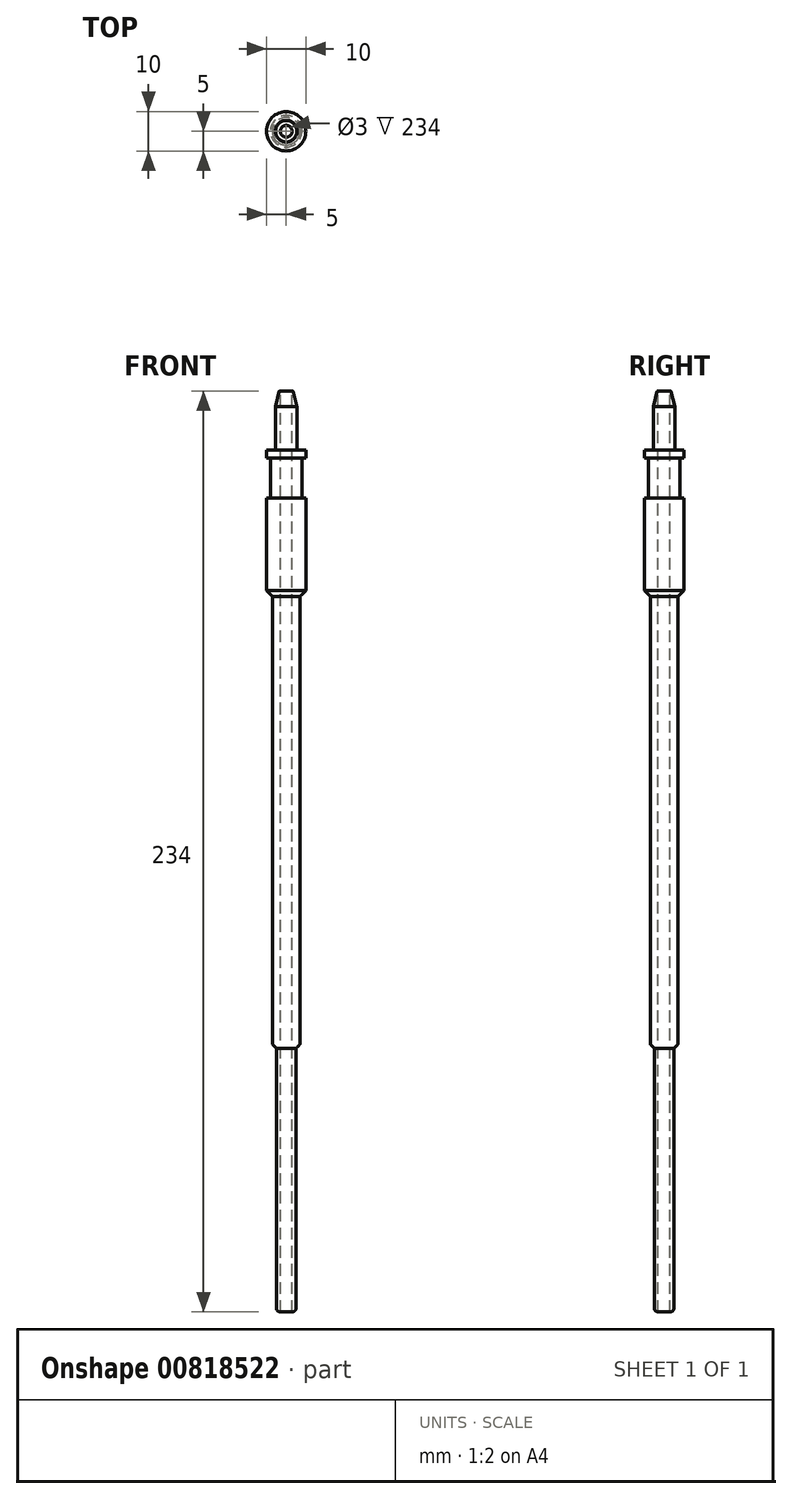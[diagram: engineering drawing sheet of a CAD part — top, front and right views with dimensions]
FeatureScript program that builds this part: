
annotation { "Feature Type Name" : "Feature", "Feature Type Description" : "" }
export const myFeature = defineFeature(function(context is Context, id is Id, definition is map)
    precondition{}
    {
        {
            var Q0;
            Q0=qCreatedBy(makeId("Front.planeOp"),FACE);
            var sketch = newSketch(context, id + "F0", { "sketchPlane" : qUnion([Q0])});
            skLineSegment(sketch, "E0", {"start": v(-1.5, 29.44) * mm, "end": v(-2.75, 28.44) * mm});
            skLineSegment(sketch, "E1", {"start": v(-2.75, 28.44) * mm, "end": v(-2.75, 14.44) * mm});
            skLineSegment(sketch, "E2", {"start": v(-2.75, 14.44) * mm, "end": v(-5, 14.44) * mm});
            skLineSegment(sketch, "E3", {"start": v(-5, 14.44) * mm, "end": v(-5, 12.44) * mm});
            skLineSegment(sketch, "E4", {"start": v(-5, 12.44) * mm, "end": v(-4, 12.44) * mm});
            skLineSegment(sketch, "E5", {"start": v(-4, 12.44) * mm, "end": v(-4, 2.24) * mm});
            skLineSegment(sketch, "E6", {"start": v(-4, 2.24) * mm, "end": v(-5, 2.24) * mm});
            skLineSegment(sketch, "E7", {"start": v(-5, 2.24) * mm, "end": v(-5, -22.26) * mm});
            skLineSegment(sketch, "E8", {"start": v(-5, -22.26) * mm, "end": v(-3.5, -23.26) * mm});
            skLineSegment(sketch, "E9", {"start": v(-3.5, -23.26) * mm, "end": v(-3.5, -136.56) * mm});
            skLineSegment(sketch, "E10", {"start": v(-3.5, -136.56) * mm, "end": v(-2.5, -137.56) * mm});
            skLineSegment(sketch, "E11", {"start": v(-2.5, -137.56) * mm, "end": v(-2.5, -204.56) * mm});
            skLineSegment(sketch, "E12", {"start": v(0, 30.64) * mm, "end": v(0, -204.56) * mm, "construction": true});
            skLineSegment(sketch, "E13", {"start": v(0, 30.64) * mm, "end": v(0, -204.56) * mm});
            skLineSegment(sketch, "E14", {"start": v(-1.5, 29.44) * mm, "end": v(-1.5, -204.56) * mm});
            skLineSegment(sketch, "E15", {"start": v(-2.5, -204.56) * mm, "end": v(0, -204.56) * mm});
            skPoint(sketch, "E16.orphan", {"position": v(0, -205.56) * mm});
            skLineSegment(sketch, "E17", {"start": v(-1.5, 29.44) * mm, "end": v(-2.75, 29.44) * mm});
            skLineSegment(sketch, "E18", {"start": v(-2.75, 29.44) * mm, "end": v(-2.75, 28.44) * mm});
            skLineSegment(sketch, "E19", {"start": v(-5, -22.26) * mm, "end": v(-5, -23.26) * mm});
            skLineSegment(sketch, "E20", {"start": v(-5, -23.26) * mm, "end": v(-3.5, -23.26) * mm});
            skSolve(sketch);
        }
        {
            var Q0;
            {var subQ0=sQuery(id+"F0.wireOp",EDGE,"E1");Q0=makeQuery(id+"F0.imprint","IMPRINT",FACE,{"disambiguationData":[TD([[makeQuery(id+"F0.imprint","IMPRINT",EDGE,{"derivedFrom":subQ0}),1.0]])]});}
            var Q1;
            Q1=makeQuery(id+"F0.imprint","IMPRINT",FACE,{"disambiguationData":[TD([[makeQuery(id+"F0.imprint","IMPRINT",EDGE,{"derivedFrom":sQuery(id+"F0.wireOp",EDGE,"E8")}),-1.0]])]});
            var Q2;
            Q2=makeQuery(id+"F0.imprint","IMPRINT",FACE,{"disambiguationData":[TD([[makeQuery(id+"F0.imprint","IMPRINT",EDGE,{"derivedFrom":sQuery(id+"F0.wireOp",EDGE,"E0")}),-1.0]])]});
            var Q3;
            Q3=sQuery(id+"F0.wireOp",EDGE,"E13");
            revolve(context, id + "F1", {"surfaceOperationType" : NewSurfaceOperationType.NEW, "entities" : qUnion([Q0, Q1, Q2]), "axis" : qUnion([Q3]), "revolveType" : RevolveType.FULL});
        }
        {
            var Q0;
            Q0=qCreatedBy(makeId("Top.planeOp"),FACE);
            cPlane(context, id + "F2", {"entities" : qUnion([Q0]), "cplaneType" : CPlaneType.OFFSET, "offset" : 30.5 * mm, "width" : 150 * mm, "height" : 150 * mm});
        }
        {
            var Q0;
            Q0=qCreatedBy(id+"F2.planeOp",FACE);
            var sketch = newSketch(context, id + "F3", { "sketchPlane" : qUnion([Q0])});
            skCircle(sketch, "E21", {"center": v(0, 0) * mm, "radius": 1.5 * mm});
            skSolve(sketch);
        }
        {
            var Q0;
            Q0=makeQuery(id+"F3.imprint","IMPRINT",FACE,{"disambiguationData":[TD([[makeQuery(id+"F3.imprint","IMPRINT",EDGE,{"derivedFrom":sQuery(id+"F3.wireOp",EDGE,"E21")}),1.0]])]});
            extrude(context, id + "F4", {"entities" : qUnion([Q0]), "operationType" : NewBodyOperationType.REMOVE, "endBound" : BoundingType.THROUGH_ALL, "oppositeDirection" : true, "depth" : 25 * mm, "offsetDistance" : 25 * mm});
        }
        {
            var Q0;
            Q0=makeQuery(id+"F1.opRevolve","SWEPT_EDGE",EDGE,{"disambiguationData":[OSD([sQuery(id+"F0.wireOp",EDGE,"E19"),sQuery(id+"F0.wireOp",EDGE,"E20")])]});
            chamfer(context, id + "F5", {"entities" : qUnion([Q0]), "width" : 2 * mm, "tangentPropagation" : true});
        }
        {
            var Q0;
            Q0=makeQuery(id+"F1.opRevolve","SWEPT_EDGE",EDGE,{"disambiguationData":[OSD([sQuery(id+"F0.wireOp",EDGE,"E17"),sQuery(id+"F0.wireOp",EDGE,"E18")])]});
            chamfer(context, id + "F6", {"entities" : qUnion([Q0]), "chamferType" : ChamferType.TWO_OFFSETS, "width1" : 1 * mm, "oppositeDirection" : false, "width2" : 4 * mm, "tangentPropagation" : true});
        }
        {
            var Q0;
            {var subQ0=sQuery(id+"F0.wireOp",EDGE,"E17");Q0=makeQuery(id+"F6.opChamfer","BLEND_EDGE",EDGE,{"blendedFrom":[makeQuery(id+"F1.opRevolve","SWEPT_EDGE",EDGE,{"disambiguationData":[OSD([subQ0,sQuery(id+"F0.wireOp",EDGE,"E18")])]}),makeQuery(id+"F1.opRevolve","SWEPT_FACE",FACE,{"disambiguationData":[OSD([subQ0])]})],"blendedInto":[makeQuery(id+"F1.opRevolve","SWEPT_FACE",FACE,{"disambiguationData":[OSD([subQ0])]})]});}
            fillet(context, id + "F7", {"entities" : qUnion([Q0]), "radius" : 0.2 * mm, "tangentPropagation" : true, "allowEdgeOverflow" : false});
        }
        {
            var Q0;
            Q0=makeQuery(id+"F1.opRevolve","SWEPT_EDGE",EDGE,{"disambiguationData":[OSD([sQuery(id+"F0.wireOp",EDGE,"E9"),sQuery(id+"F0.wireOp",EDGE,"E10")])]});
            fillet(context, id + "F8", {"entities" : qUnion([Q0]), "radius" : 0.5 * mm, "tangentPropagation" : true, "allowEdgeOverflow" : false});
        }
        {
            var Q0;
            Q0=makeQuery(id+"F1.opRevolve","SWEPT_EDGE",EDGE,{"disambiguationData":[OSD([sQuery(id+"F0.wireOp",EDGE,"E11"),sQuery(id+"F0.wireOp",EDGE,"E15")])]});
            fillet(context, id + "F9", {"entities" : qUnion([Q0]), "radius" : 1 * mm, "tangentPropagation" : true, "allowEdgeOverflow" : false});
        }
    });
